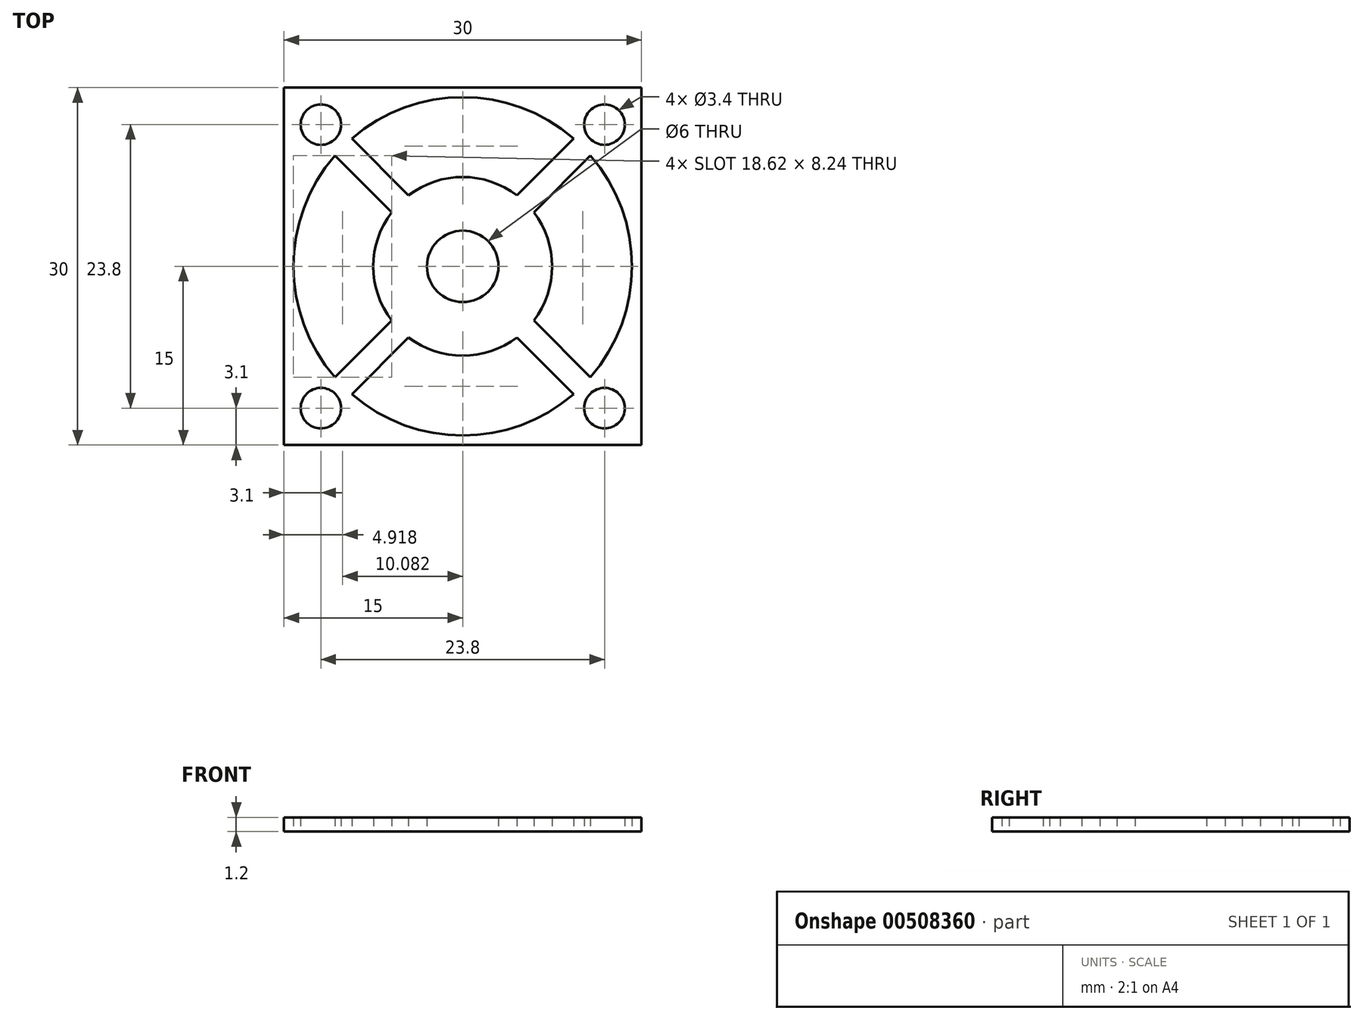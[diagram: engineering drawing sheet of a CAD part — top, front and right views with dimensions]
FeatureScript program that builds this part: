
annotation { "Feature Type Name" : "Feature", "Feature Type Description" : "" }
export const myFeature = defineFeature(function(context is Context, id is Id, definition is map)
    precondition{}
    {
        {
            var Q0;
            Q0=qCreatedBy(makeId("Top.planeOp"),FACE);
            var sketch = newSketch(context, id + "F0", { "sketchPlane" : qUnion([Q0])});
            skLineSegment(sketch, "E0.bottom", {"start": v(15, 15) * mm, "end": v(-15, 15) * mm});
            skLineSegment(sketch, "E0.top", {"start": v(15, -15) * mm, "end": v(-15, -15) * mm});
            skLineSegment(sketch, "E0.left", {"start": v(15, 15) * mm, "end": v(15, -15) * mm});
            skLineSegment(sketch, "E0.right", {"start": v(-15, 15) * mm, "end": v(-15, -15) * mm});
            skPoint(sketch, "E0.middle", {"position": v(0, 0) * mm});
            skCircle(sketch, "E1", {"center": v(-11.9, 11.9) * mm, "radius": 1.7 * mm});
            skLineSegment(sketch, "E2", {"start": v(0, 2.57) * mm, "end": v(0, -2.44) * mm, "construction": true});
            skLineSegment(sketch, "E3", {"start": v(-2.9, 0) * mm, "end": v(2.33, 0) * mm, "construction": true});
            skCircle(sketch, "E4.MirrorC", {"center": v(11.9, 11.9) * mm, "radius": 1.7 * mm});
            skCircle(sketch, "E5.MirrorC", {"center": v(-11.9, -11.9) * mm, "radius": 1.7 * mm});
            skCircle(sketch, "E6.MirrorC", {"center": v(11.9, -11.9) * mm, "radius": 1.7 * mm});
            skArc(sketch, "E7", {"start": v(10.72, -9.3) * mm, "mid": v(14.2, 0) * mm, "end": v(10.72, 9.3) * mm});
            skLineSegment(sketch, "E8", {"start": v(-10.72, -9.3) * mm, "end": v(-5.96, -4.55) * mm});
            skLineSegment(sketch, "E9", {"start": v(-9.3, -10.72) * mm, "end": v(-4.55, -5.96) * mm});
            skLineSegment(sketch, "E10.MirrorCS", {"start": v(10.72, -9.3) * mm, "end": v(5.96, -4.55) * mm});
            skLineSegment(sketch, "E11.MirrorCS", {"start": v(9.3, -10.72) * mm, "end": v(4.55, -5.96) * mm});
            skPoint(sketch, "E12.orphan", {"position": v(-10.22, -11.63) * mm});
            skPoint(sketch, "E13.orphan", {"position": v(-11.63, -10.22) * mm});
            skPoint(sketch, "E14.orphan", {"position": v(-10.22, 11.63) * mm});
            skPoint(sketch, "E15.orphan", {"position": v(-13.58, 12.17) * mm});
            skPoint(sketch, "E16.orphan", {"position": v(10.22, 11.63) * mm});
            skPoint(sketch, "E17.orphan", {"position": v(13.58, 12.17) * mm});
            skPoint(sketch, "E18.orphan", {"position": v(11.63, -10.22) * mm});
            skPoint(sketch, "E19.orphan", {"position": v(10.22, -11.63) * mm});
            skLineSegment(sketch, "E20.trimOffspring", {"start": v(1.41, 0) * mm, "end": v(2.7, 1.3) * mm});
            skLineSegment(sketch, "E21.trimOffspring", {"start": v(-1.41, 0) * mm, "end": v(-2.7, 1.3) * mm});
            skLineSegment(sketch, "E22.trimOffspring", {"start": v(0, 1.41) * mm, "end": v(1.3, 2.7) * mm});
            skLineSegment(sketch, "E23.trimOffspring", {"start": v(0, 1.41) * mm, "end": v(-1.3, 2.7) * mm});
            skLineSegment(sketch, "E24", {"start": v(-12.6, -11.2) * mm, "end": v(-11.2, -12.6) * mm, "construction": true});
            skArc(sketch, "E25", {"start": v(-4.55, -5.96) * mm, "mid": v(0, -7.5) * mm, "end": v(4.55, -5.96) * mm});
            skCircle(sketch, "E26", {"center": v(0, 0) * mm, "radius": 3 * mm});
            skLineSegment(sketch, "E27.trimOffspring", {"start": v(-5.96, 4.55) * mm, "end": v(-10.72, 9.3) * mm});
            skLineSegment(sketch, "E28.trimOffspring", {"start": v(-4.55, 5.96) * mm, "end": v(-9.3, 10.72) * mm});
            skLineSegment(sketch, "E29.trimOffspring", {"start": v(4.55, 5.96) * mm, "end": v(9.3, 10.72) * mm});
            skLineSegment(sketch, "E30.trimOffspring", {"start": v(5.96, 4.55) * mm, "end": v(10.72, 9.3) * mm});
            skLineSegment(sketch, "E31.trimOffspring", {"start": v(2.7, -1.3) * mm, "end": v(1.41, 0) * mm});
            skLineSegment(sketch, "E32.trimOffspring", {"start": v(1.3, -2.7) * mm, "end": v(0, -1.41) * mm});
            skLineSegment(sketch, "E33.trimOffspring", {"start": v(-2.7, -1.3) * mm, "end": v(-1.41, 0) * mm});
            skLineSegment(sketch, "E34.trimOffspring", {"start": v(-1.3, -2.7) * mm, "end": v(0, -1.41) * mm});
            skArc(sketch, "E35.trimOffspring", {"start": v(-5.96, 4.55) * mm, "mid": v(-7.5, 0) * mm, "end": v(-5.96, -4.55) * mm});
            skArc(sketch, "E36.trimOffspring", {"start": v(4.55, 5.96) * mm, "mid": v(0, 7.5) * mm, "end": v(-4.55, 5.96) * mm});
            skArc(sketch, "E37.trimOffspring", {"start": v(5.96, -4.55) * mm, "mid": v(7.5, 0) * mm, "end": v(5.96, 4.55) * mm});
            skArc(sketch, "E38.trimOffspring", {"start": v(9.3, 10.72) * mm, "mid": v(0, 14.2) * mm, "end": v(-9.3, 10.72) * mm});
            skArc(sketch, "E39.trimOffspring", {"start": v(-10.72, 9.3) * mm, "mid": v(-14.2, 0) * mm, "end": v(-10.72, -9.3) * mm});
            skArc(sketch, "E40.trimOffspring", {"start": v(-9.3, -10.72) * mm, "mid": v(0, -14.2) * mm, "end": v(9.3, -10.72) * mm});
            skSolve(sketch);
        }
        {
            var Q0;
            Q0=makeQuery(id+"F0.imprint","IMPRINT",FACE,{"disambiguationData":[TD([[makeQuery(id+"F0.imprint","IMPRINT",EDGE,{"derivedFrom":sQuery(id+"F0.wireOp",EDGE,"E0.bottom")}),1.0]])]});
            extrude(context, id + "F1", {"entities" : qUnion([Q0]), "depth" : 1.2 * mm});
        }
    });
